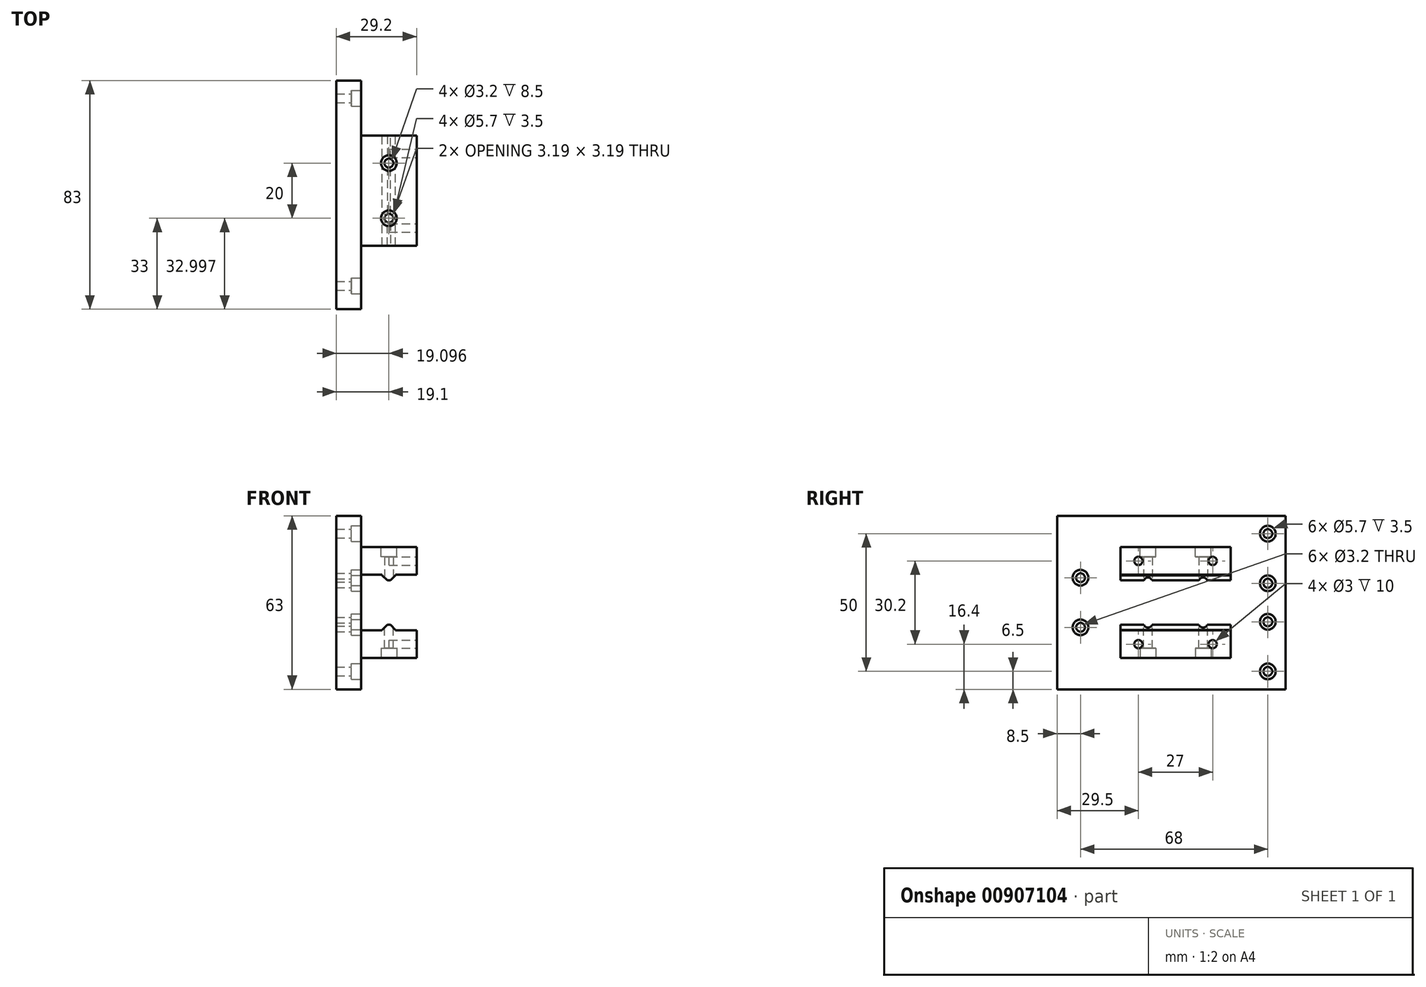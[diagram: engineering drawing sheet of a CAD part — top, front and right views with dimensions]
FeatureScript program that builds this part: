
annotation { "Feature Type Name" : "Feature", "Feature Type Description" : "" }
export const myFeature = defineFeature(function(context is Context, id is Id, definition is map)
    precondition{}
    {
        {
            assignVariable(context, id + "F0", {"name" : "headdepth", "anyValue" : 3.5 * mm});
        }
        {
            var Q0;
            Q0=qCreatedBy(makeId("Top.planeOp"),FACE);
            var sketch = newSketch(context, id + "F1", { "sketchPlane" : qUnion([Q0])});
            skLineSegment(sketch, "E0.bottom", {"start": v(0, 0) * mm, "end": v(9, 0) * mm});
            skLineSegment(sketch, "E0.top", {"start": v(0, 83) * mm, "end": v(9, 83) * mm});
            skLineSegment(sketch, "E0.left", {"start": v(0, 0) * mm, "end": v(0, 83) * mm});
            skLineSegment(sketch, "E0.right", {"start": v(9, 0) * mm, "end": v(9, 83) * mm});
            skSolve(sketch);
        }
        {
            var Q0;
            Q0=qSketchRegion(id+"F1",true);
            var Q1;
            Q1=makeQuery(id+"F1.imprint","IMPRINT",FACE,{"disambiguationData":[TD([[makeQuery(id+"F1.imprint","IMPRINT",EDGE,{"derivedFrom":sQuery(id+"F1.wireOp",EDGE,"E0.bottom")}),1.0]])]});
            extrude(context, id + "F2", {"entities" : qUnion([Q0, Q1]), "depth" : 63 * mm, "offsetDistance" : 25 * mm});
        }
        {
            var Q0;
            Q0=makeQuery(id+"F2.opExtrude","SWEPT_FACE",FACE,{"disambiguationData":[OSD([sQuery(id+"F1.wireOp",EDGE,"E0.right")])]});
            var sketch = newSketch(context, id + "F3", { "sketchPlane" : qUnion([Q0])});
            skLineSegment(sketch, "E1", {"start": v(83, 6.5) * mm, "end": v(0, 6.5) * mm, "construction": true});
            skLineSegment(sketch, "E2", {"start": v(0, 24.5) * mm, "end": v(83, 24.5) * mm, "construction": true});
            skLineSegment(sketch, "E3", {"start": v(83, 38.5) * mm, "end": v(0, 38.5) * mm, "construction": true});
            skLineSegment(sketch, "E4", {"start": v(0, 56.5) * mm, "end": v(83, 56.5) * mm, "construction": true});
            skLineSegment(sketch, "E5", {"start": v(76.5, 63) * mm, "end": v(76.5, 0) * mm, "construction": true});
            skLineSegment(sketch, "E6", {"start": v(8.5, 63) * mm, "end": v(8.5, 0) * mm, "construction": true});
            skLineSegment(sketch, "E7", {"start": v(0, 22.5) * mm, "end": v(8.5, 22.5) * mm, "construction": true});
            skLineSegment(sketch, "E8", {"start": v(0, 40.5) * mm, "end": v(8.5, 40.5) * mm, "construction": true});
            skCircle(sketch, "E9", {"center": v(8.5, 40.5) * mm, "radius": 2.85 * mm});
            skCircle(sketch, "E10", {"center": v(8.5, 22.5) * mm, "radius": 2.85 * mm});
            skCircle(sketch, "E11", {"center": v(76.5, 56.5) * mm, "radius": 2.85 * mm});
            skCircle(sketch, "E12", {"center": v(76.5, 38.5) * mm, "radius": 2.85 * mm});
            skCircle(sketch, "E13", {"center": v(76.5, 24.5) * mm, "radius": 2.85 * mm});
            skCircle(sketch, "E14", {"center": v(76.5, 6.5) * mm, "radius": 2.85 * mm});
            skSolve(sketch);
        }
        {
            var Q0;
            Q0=qSketchRegion(id+"F3",true);
            var Q1;
            Q1=makeQuery(id+"F3.imprint","IMPRINT",FACE,{"disambiguationData":[TD([[makeQuery(id+"F3.imprint","IMPRINT",EDGE,{"derivedFrom":sQuery(id+"F3.wireOp",EDGE,"E9")}),1.0]])]});
            extrude(context, id + "F4", {"entities" : qUnion([Q0, Q1]), "operationType" : NewBodyOperationType.REMOVE, "oppositeDirection" : true, "depth" : getVariable(context, 'headdepth'), "offsetDistance" : 25 * mm});
        }
        {
            var Q0;
            Q0=makeQuery(id+"F3.imprint","IMPRINT",FACE,{"disambiguationData":[TD([[makeQuery(id+"F3.imprint","IMPRINT",EDGE,{"derivedFrom":sQuery(id+"F3.wireOp",EDGE,"E9")}),1.0]])]});
            var sketch = newSketch(context, id + "F5", { "sketchPlane" : qUnion([Q0])});
            skCircle(sketch, "E15", {"center": v(8.5, 40.5) * mm, "radius": 1.6 * mm});
            skCircle(sketch, "E16", {"center": v(8.5, 22.5) * mm, "radius": 1.6 * mm});
            skCircle(sketch, "E17", {"center": v(76.5, 24.5) * mm, "radius": 1.6 * mm});
            skCircle(sketch, "E18", {"center": v(76.5, 38.5) * mm, "radius": 1.6 * mm});
            skCircle(sketch, "E19", {"center": v(76.5, 56.5) * mm, "radius": 1.6 * mm});
            skCircle(sketch, "E20", {"center": v(76.5, 6.5) * mm, "radius": 1.6 * mm});
            skSolve(sketch);
        }
        {
            var Q0;
            Q0=qSketchRegion(id+"F5",true);
            extrude(context, id + "F6", {"entities" : qUnion([Q0]), "operationType" : NewBodyOperationType.REMOVE, "oppositeDirection" : true, "depth" : 25 * mm, "offsetDistance" : 25 * mm});
        }
        {
            var Q0;
            Q0=makeQuery(id+"F2.opExtrude","SWEPT_FACE",FACE,{"disambiguationData":[OSD([sQuery(id+"F1.wireOp",EDGE,"E0.right")])]});
            var sketch = newSketch(context, id + "F7", { "sketchPlane" : qUnion([Q0])});
            skLineSegment(sketch, "E21", {"start": v(83, 31.5) * mm, "end": v(0, 31.5) * mm, "construction": true});
            skLineSegment(sketch, "E22.bottom", {"start": v(63, 41.6) * mm, "end": v(23, 41.6) * mm});
            skLineSegment(sketch, "E22.top", {"start": v(63, 51.6) * mm, "end": v(23, 51.6) * mm});
            skLineSegment(sketch, "E22.left", {"start": v(63, 41.6) * mm, "end": v(63, 51.6) * mm});
            skLineSegment(sketch, "E22.right", {"start": v(23, 41.6) * mm, "end": v(23, 51.6) * mm});
            skLineSegment(sketch, "E23.MirrorCS", {"start": v(63, 21.4) * mm, "end": v(63, 11.4) * mm});
            skLineSegment(sketch, "E24.MirrorCS", {"start": v(63, 21.4) * mm, "end": v(23, 21.4) * mm});
            skLineSegment(sketch, "E25.MirrorCS", {"start": v(63, 11.4) * mm, "end": v(23, 11.4) * mm});
            skLineSegment(sketch, "E26.MirrorCS", {"start": v(23, 21.4) * mm, "end": v(23, 11.4) * mm});
            skSolve(sketch);
        }
        {
            var Q0;
            Q0=makeQuery(id+"F7.imprint","IMPRINT",FACE,{"disambiguationData":[TD([[makeQuery(id+"F7.imprint","IMPRINT",EDGE,{"derivedFrom":sQuery(id+"F7.wireOp",EDGE,"E23.MirrorCS")}),-1.0]])]});
            var Q1;
            Q1=makeQuery(id+"F7.imprint","IMPRINT",FACE,{"disambiguationData":[TD([[makeQuery(id+"F7.imprint","IMPRINT",EDGE,{"derivedFrom":sQuery(id+"F7.wireOp",EDGE,"E22.bottom")}),-1.0]])]});
            extrude(context, id + "F8", {"entities" : qUnion([Q0, Q1]), "operationType" : NewBodyOperationType.ADD, "depth" : 20.2 * mm, "offsetDistance" : 25 * mm});
        }
        {
            var Q0;
            Q0=makeQuery(id+"F8.opExtrude","SWEPT_FACE",FACE,{"disambiguationData":[OSD([sQuery(id+"F7.wireOp",EDGE,"E22.bottom")])]});
            var sketch = newSketch(context, id + "F9", { "sketchPlane" : qUnion([Q0])});
            skLineSegment(sketch, "E27", {"start": v(19.1, -23) * mm, "end": v(19.1, -63) * mm, "construction": true});
            skLineSegment(sketch, "E28.bottom", {"start": v(21.5, -23) * mm, "end": v(16.7, -23) * mm});
            skLineSegment(sketch, "E28.top", {"start": v(21.5, -63) * mm, "end": v(16.7, -63) * mm});
            skLineSegment(sketch, "E28.left", {"start": v(21.5, -23) * mm, "end": v(21.5, -63) * mm});
            skLineSegment(sketch, "E28.right", {"start": v(16.7, -23) * mm, "end": v(16.7, -63) * mm});
            skSolve(sketch);
        }
        {
            var Q0;
            Q0 = qSketchRegion(id + "F9", true);
            extrude(context, id + "F10", {"entities" : qUnion([Q0]), "operationType" : NewBodyOperationType.ADD, "depth" : 2 * mm, "offsetDistance" : 25 * mm});
        }
        {
            var Q0;
            Q0=makeQuery(id+"F10.opExtrude","CAP_EDGE",EDGE,{"disambiguationData":[OSD([sQuery(id+"F9.wireOp",EDGE,"E28.left")])],"isStart":false});
            var Q1;
            Q1=makeQuery(id+"F10.opExtrude","CAP_EDGE",EDGE,{"disambiguationData":[OSD([sQuery(id+"F9.wireOp",EDGE,"E28.right")])],"isStart":false});
            chamfer(context, id + "F11", {"entities" : qUnion([Q0, Q1]), "width" : 1.8 * mm, "tangentPropagation" : true});
        }
        {
            var Q0;
            Q0=makeQuery(id+"F10.opExtrude","CAP_FACE",FACE,{"disambiguationData":[OSD([sQuery(id+"F9.wireOp",EDGE,"E28.bottom"),sQuery(id+"F9.wireOp",EDGE,"E28.top"),sQuery(id+"F9.wireOp",EDGE,"E28.left"),sQuery(id+"F9.wireOp",EDGE,"E28.right")])],"isStart":false});
            var sketch = newSketch(context, id + "F12", { "sketchPlane" : qUnion([Q0])});
            skLineSegment(sketch, "E29", {"start": v(19.1, -23) * mm, "end": v(19.1, -63) * mm, "construction": true});
            skCircle(sketch, "E30", {"center": v(19.1, -33) * mm, "radius": 1.6 * mm});
            skCircle(sketch, "E31", {"center": v(19.1, -53) * mm, "radius": 1.6 * mm});
            skSolve(sketch);
        }
        {
            var Q0;
            Q0 = qSketchRegion(id + "F12", true);
            extrude(context, id + "F13", {"entities" : qUnion([Q0]), "operationType" : NewBodyOperationType.REMOVE, "oppositeDirection" : true, "depth" : 25 * mm, "offsetDistance" : 25 * mm});
        }
        {
            var Q0;
            Q0=makeQuery(id+"F8.opExtrude","SWEPT_FACE",FACE,{"disambiguationData":[OSD([sQuery(id+"F7.wireOp",EDGE,"E24.MirrorCS")])]});
            var sketch = newSketch(context, id + "F14", { "sketchPlane" : qUnion([Q0])});
            skLineSegment(sketch, "E32", {"start": v(19.1, 63) * mm, "end": v(19.1, 23) * mm, "construction": true});
            skLineSegment(sketch, "E33.bottom", {"start": v(21.5, 23) * mm, "end": v(16.7, 23) * mm});
            skLineSegment(sketch, "E33.top", {"start": v(21.5, 63) * mm, "end": v(16.7, 63) * mm});
            skLineSegment(sketch, "E33.left", {"start": v(21.5, 23) * mm, "end": v(21.5, 63) * mm});
            skLineSegment(sketch, "E33.right", {"start": v(16.7, 23) * mm, "end": v(16.7, 63) * mm});
            skSolve(sketch);
        }
        {
            var Q0;
            Q0 = qSketchRegion(id + "F14", true);
            extrude(context, id + "F15", {"entities" : qUnion([Q0]), "operationType" : NewBodyOperationType.ADD, "depth" : 2 * mm, "offsetDistance" : 25 * mm});
        }
        {
            var Q0;
            Q0=makeQuery(id+"F15.opExtrude","CAP_EDGE",EDGE,{"disambiguationData":[OSD([sQuery(id+"F14.wireOp",EDGE,"E33.left")])],"isStart":false});
            var Q1;
            Q1=makeQuery(id+"F15.opExtrude","CAP_EDGE",EDGE,{"disambiguationData":[OSD([sQuery(id+"F14.wireOp",EDGE,"E33.right")])],"isStart":false});
            chamfer(context, id + "F16", {"entities" : qUnion([Q0, Q1]), "width" : 1.8 * mm, "tangentPropagation" : true});
        }
        {
            var Q0;
            Q0=makeQuery(id+"F15.opExtrude","CAP_FACE",FACE,{"disambiguationData":[OSD([sQuery(id+"F14.wireOp",EDGE,"E33.bottom"),sQuery(id+"F14.wireOp",EDGE,"E33.top"),sQuery(id+"F14.wireOp",EDGE,"E33.left"),sQuery(id+"F14.wireOp",EDGE,"E33.right")])],"isStart":false});
            var sketch = newSketch(context, id + "F17", { "sketchPlane" : qUnion([Q0])});
            skLineSegment(sketch, "E34", {"start": v(19.1, 63) * mm, "end": v(19.1, 23) * mm, "construction": true});
            skCircle(sketch, "E35", {"center": v(19.1, 33) * mm, "radius": 1.6 * mm});
            skCircle(sketch, "E36", {"center": v(19.1, 53) * mm, "radius": 1.6 * mm});
            skSolve(sketch);
        }
        {
            var Q0;
            Q0 = qSketchRegion(id + "F17", true);
            extrude(context, id + "F18", {"entities" : qUnion([Q0]), "operationType" : NewBodyOperationType.REMOVE, "oppositeDirection" : true, "depth" : 25 * mm, "offsetDistance" : 25 * mm});
        }
        {
            var Q0;
            Q0=makeQuery(id+"F8.opExtrude","SWEPT_FACE",FACE,{"disambiguationData":[OSD([sQuery(id+"F7.wireOp",EDGE,"E25.MirrorCS")])]});
            var sketch = newSketch(context, id + "F19", { "sketchPlane" : qUnion([Q0])});
            skCircle(sketch, "E37", {"center": v(19.1, -33) * mm, "radius": 2.85 * mm});
            skCircle(sketch, "E38", {"center": v(19.1, -53) * mm, "radius": 2.85 * mm});
            skSolve(sketch);
        }
        {
            var Q0;
            Q0 = qSketchRegion(id + "F19", true);
            extrude(context, id + "F20", {"entities" : qUnion([Q0]), "operationType" : NewBodyOperationType.REMOVE, "oppositeDirection" : true, "depth" : 3.5 * mm, "offsetDistance" : 25 * mm});
        }
        {
            var Q0;
            Q0=makeQuery(id+"F8.opExtrude","SWEPT_FACE",FACE,{"disambiguationData":[OSD([sQuery(id+"F7.wireOp",EDGE,"E22.top")])]});
            var sketch = newSketch(context, id + "F21", { "sketchPlane" : qUnion([Q0])});
            skCircle(sketch, "E39", {"center": v(19.1, 53) * mm, "radius": 2.85 * mm});
            skCircle(sketch, "E40", {"center": v(19.1, 33) * mm, "radius": 2.85 * mm});
            skSolve(sketch);
        }
        {
            var Q0;
            Q0 = qSketchRegion(id + "F21", true);
            extrude(context, id + "F22", {"entities" : qUnion([Q0]), "operationType" : NewBodyOperationType.REMOVE, "oppositeDirection" : true, "depth" : 3.5 * mm, "offsetDistance" : 25 * mm});
        }
        {
            var Q0;
            Q0=makeQuery(id+"F8.opExtrude","CAP_FACE",FACE,{"disambiguationData":[OSD([sQuery(id+"F7.wireOp",EDGE,"E23.MirrorCS"),sQuery(id+"F7.wireOp",EDGE,"E24.MirrorCS"),sQuery(id+"F7.wireOp",EDGE,"E25.MirrorCS"),sQuery(id+"F7.wireOp",EDGE,"E26.MirrorCS")])],"isStart":false});
            var sketch = newSketch(context, id + "F23", { "sketchPlane" : qUnion([Q0])});
            skLineSegment(sketch, "E41", {"start": v(63, 16.4) * mm, "end": v(23, 16.4) * mm, "construction": true});
            skLineSegment(sketch, "E42", {"start": v(56.5, 11.4) * mm, "end": v(56.5, 21.4) * mm, "construction": true});
            skLineSegment(sketch, "E43", {"start": v(43, 11.4) * mm, "end": v(43, 21.4) * mm, "construction": true});
            skLineSegment(sketch, "E44", {"start": v(29.5, 11.4) * mm, "end": v(29.5, 21.4) * mm, "construction": true});
            skCircle(sketch, "E45", {"center": v(56.5, 16.4) * mm, "radius": 1.5 * mm});
            skCircle(sketch, "E46", {"center": v(29.5, 16.4) * mm, "radius": 1.5 * mm});
            skCircle(sketch, "E47.MirrorC", {"center": v(29.5, 46.6) * mm, "radius": 1.5 * mm});
            skCircle(sketch, "E48.MirrorC", {"center": v(56.5, 46.6) * mm, "radius": 1.5 * mm});
            skSolve(sketch);
        }
        {
            var Q0;
            Q0 = qSketchRegion(id + "F23", true);
            extrude(context, id + "F24", {"entities" : qUnion([Q0]), "operationType" : NewBodyOperationType.REMOVE, "oppositeDirection" : true, "depth" : 10 * mm, "offsetDistance" : 25 * mm});
        }
    });
